# Revit family: РОСМА_МанометрИзмеренияНизкихДавлГазов
name_source: partatom
category: Арматура трубопроводов
revit_build: Autodesk Revit 2018 (Build: 20180423_1000(x64)
units: mm (PartAtom-declared; Revit-internal decimal feet)

## family parameters
Всегда вертикально = Да
На основе рабочей плоскости = Нет
Общий = Нет
При загрузке вырезать с полостями = Нет
Размер круглого соединителя = Использовать диаметр
Тип детали = Вставляется

## types (4) — shared parameters
ADSK_Единица измерения = шт.
ADSK_Количество = 1
Table = спец_для измерения низких давлений газов
Table_2 = размеры_для измерения низких давлений газов
URL = https://rosma.spb.ru
Группа модели = Оборудование
Давление01 = ‎ : КМ 0…2.5кПа
Давление02 = ‎ : КМ 0…4кПа
Давление03 = ‎ : КМ 0…6кПа
Давление04 = ‎ : КМ 0…10кПа
Давление05 = ‎ : КМ 0…16кПа
Давление06 = ‎ : КМ 0…25кПа
Давление07 = ‎ : КМ 0…40кПа
Давление08 = ‎ : КМ 0…60кПа
Давление09 = ‎ : КМВ -1…1.5кПа
Давление10 = ‎ : КМВ -1…3кПа
Давление11 = ‎ : КМВ -0.8…0.8кПа
Давление12 = ‎ : КМВ -1.25…1.25кПа
Давление13 = ‎ : КМВ -5…5кПа
Давление14 = ‎ : КМВ -8…8кПа
Давление15 = ‎ : КМВ -12.5…12.5кПа
Изготовитель = ЗАО "РОСМА"
Климатическое исполнение = Группа С2 по ГОСТ Р 52931; климатическое исполнение УХЛ категории 3.1 по ГОСТ 15150
Код IP = IP40
Межповерочный интервал = 2 года
Описание = Тип КМ. Напоромер (манометр КМ или манометр низкого давления) применяется для измерения давления сухих, газообразных сред, неагрессивных к медным сплавам.
Техническая документация = ТУ 4212-001-4719015564-2008; ГОСТ 2405–88
лого_задн_стенка = Да

## per-type parameters (varying)
| type | DN | Ddempfer | Класс точности | Материал корпуса |
| 11 | 8.00 мм | 4 мм | 2,5 | _Краска черная глянцевая |
| 12 | 8.00 мм | 4 мм | 1,5 | _Краска Белый металлик |
| 22 | 15.00 мм | 5 мм | 1,5 | _Краска Белый металлик |
| 31 | 15.00 мм | 5 мм | 1,5 | _Краска черная глянцевая |

note: column(s) folded — value = type name in every type: Исполнение
